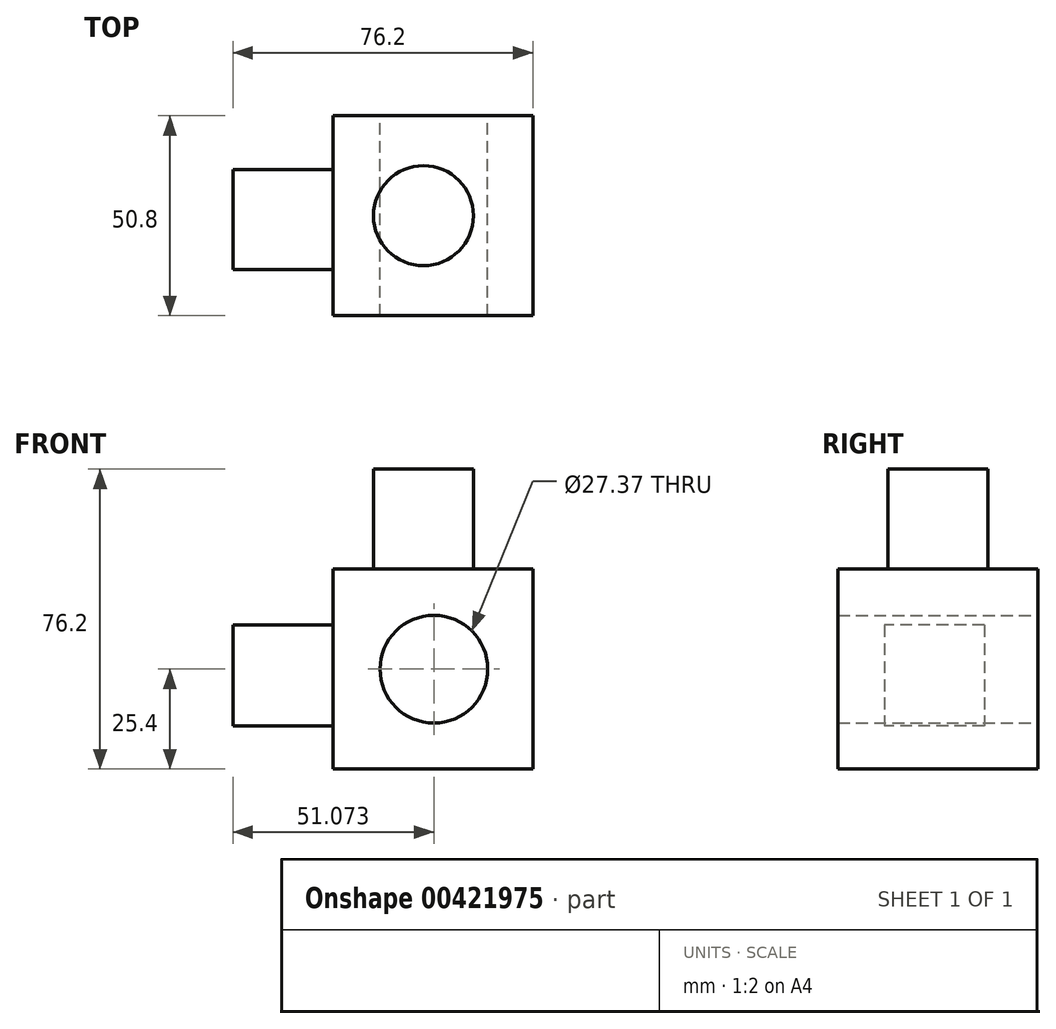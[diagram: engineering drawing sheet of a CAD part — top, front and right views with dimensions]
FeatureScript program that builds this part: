
annotation { "Feature Type Name" : "Feature", "Feature Type Description" : "" }
export const myFeature = defineFeature(function(context is Context, id is Id, definition is map)
    precondition{}
    {
        {
            var Q0;
            Q0=qCreatedBy(makeId("Front.planeOp"),FACE);
            var sketch = newSketch(context, id + "F0", { "sketchPlane" : qUnion([Q0])});
            skLineSegment(sketch, "E0.bottom", {"start": v(0, 0) * mm, "end": v(-50.8, 0) * mm});
            skLineSegment(sketch, "E0.top", {"start": v(0, 50.8) * mm, "end": v(-50.8, 50.8) * mm});
            skLineSegment(sketch, "E0.left", {"start": v(0, 0) * mm, "end": v(0, 50.8) * mm});
            skLineSegment(sketch, "E0.right", {"start": v(-50.8, 0) * mm, "end": v(-50.8, 50.8) * mm});
            skCircle(sketch, "E1", {"center": v(-26.23, 23.8) * mm, "radius": 12.7 * mm});
            skSolve(sketch);
        }
        {
            var Q0;
            Q0 = qSketchRegion(id + "F0", true);
            var Q1;
            Q1=makeQuery(id+"F0.imprint","IMPRINT",FACE,{"disambiguationData":[TD([[makeQuery(id+"F0.imprint","IMPRINT",EDGE,{"derivedFrom":sQuery(id+"F0.wireOp",EDGE,"E1")}),1.0]])]});
            extrude(context, id + "F1", {"entities" : qUnion([Q0, Q1]), "depth" : 50.8 * mm});
        }
        {
            var Q0;
            Q0=makeQuery(id+"F1.opExtrude","CAP_FACE",FACE,{"disambiguationData":[OSD([sQuery(id+"F0.wireOp",EDGE,"E0.bottom"),sQuery(id+"F0.wireOp",EDGE,"E0.top"),sQuery(id+"F0.wireOp",EDGE,"E0.left"),sQuery(id+"F0.wireOp",EDGE,"E0.right")])],"isStart":true});
            var sketch = newSketch(context, id + "F2", { "sketchPlane" : qUnion([Q0])});
            skCircle(sketch, "E2", {"center": v(25.13, 25.4) * mm, "radius": 13.68 * mm});
            skPoint(sketch, "E2.centerSnap0", {"position": v(0, 25.4) * mm});
            skSolve(sketch);
        }
        {
            var Q0;
            Q0=makeQuery(id+"F2.imprint","IMPRINT",FACE,{"disambiguationData":[TD([[makeQuery(id+"F2.imprint","IMPRINT",EDGE,{"derivedFrom":sQuery(id+"F2.wireOp",EDGE,"E2")}),1.0]])]});
            extrude(context, id + "F3", {"entities" : qUnion([Q0]), "operationType" : NewBodyOperationType.REMOVE, "oppositeDirection" : true, "depth" : 25.4 * mm});
        }
        {
            var Q0;
            Q0=makeQuery(id+"F3.boolean.opBoolean","COPY",FACE,{"derivedFrom":makeQuery(id+"F3.opExtrude","CAP_FACE",FACE,{"disambiguationData":[OSD([sQuery(id+"F2.wireOp",EDGE,"E2")])],"isStart":false})});
            extrude(context, id + "F4", {"entities" : qUnion([Q0]), "operationType" : NewBodyOperationType.REMOVE, "oppositeDirection" : true, "depth" : 25.4 * mm});
        }
        {
            var Q0;
            Q0=makeQuery(id+"F1.opExtrude","SWEPT_FACE",FACE,{"disambiguationData":[OSD([sQuery(id+"F0.wireOp",EDGE,"E0.right")])]});
            var sketch = newSketch(context, id + "F5", { "sketchPlane" : qUnion([Q0])});
            skLineSegment(sketch, "E3.bottom", {"start": v(13.61, 36.59) * mm, "end": v(39.01, 36.59) * mm});
            skLineSegment(sketch, "E3.top", {"start": v(13.61, 11.02) * mm, "end": v(39.01, 11.02) * mm});
            skLineSegment(sketch, "E3.left", {"start": v(13.61, 36.59) * mm, "end": v(13.61, 11.02) * mm});
            skLineSegment(sketch, "E3.right", {"start": v(39.01, 36.59) * mm, "end": v(39.01, 11.02) * mm});
            skPoint(sketch, "E3.middle", {"position": v(26.31, 23.8) * mm});
            skSolve(sketch);
        }
        {
            var Q0;
            Q0=makeQuery(id+"F5.imprint","IMPRINT",FACE,{"disambiguationData":[TD([[makeQuery(id+"F5.imprint","IMPRINT",EDGE,{"derivedFrom":sQuery(id+"F5.wireOp",EDGE,"E3.bottom")}),-1.0]])]});
            extrude(context, id + "F6", {"entities" : qUnion([Q0]), "operationType" : NewBodyOperationType.ADD, "depth" : 25.4 * mm});
        }
        {
            var Q0;
            Q0=makeQuery(id+"F1.opExtrude","SWEPT_FACE",FACE,{"disambiguationData":[OSD([sQuery(id+"F0.wireOp",EDGE,"E0.top")])]});
            var sketch = newSketch(context, id + "F7", { "sketchPlane" : qUnion([Q0])});
            skCircle(sketch, "E4", {"center": v(-27.77, -25.4) * mm, "radius": 12.7 * mm});
            skPoint(sketch, "E4.centerSnap0", {"position": v(-50.8, -25.4) * mm});
            skSolve(sketch);
        }
        {
            var Q0;
            Q0=makeQuery(id+"F7.imprint","IMPRINT",FACE,{"disambiguationData":[TD([[makeQuery(id+"F7.imprint","IMPRINT",EDGE,{"derivedFrom":sQuery(id+"F7.wireOp",EDGE,"E4")}),1.0]])]});
            extrude(context, id + "F8", {"entities" : qUnion([Q0]), "operationType" : NewBodyOperationType.ADD, "depth" : 25.4 * mm});
        }
    });
